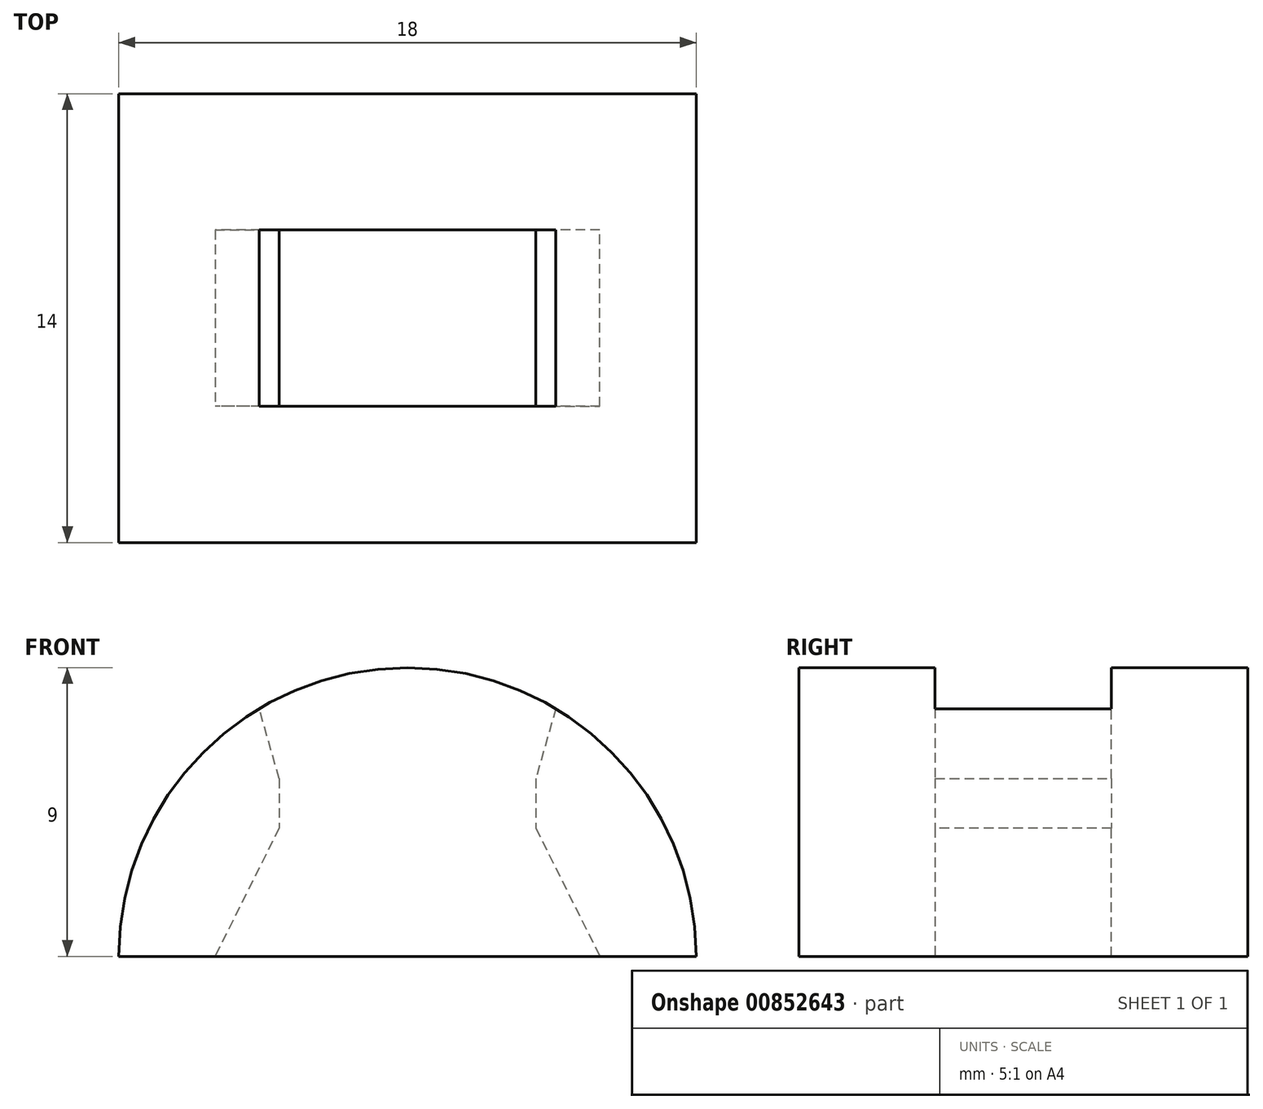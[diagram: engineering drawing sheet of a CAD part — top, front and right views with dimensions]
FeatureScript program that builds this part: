
annotation { "Feature Type Name" : "Feature", "Feature Type Description" : "" }
export const myFeature = defineFeature(function(context is Context, id is Id, definition is map)
    precondition{}
    {
        {
            var Q0;
            Q0=qCreatedBy(makeId("Top.planeOp"),FACE);
            var sketch = newSketch(context, id + "F0", { "sketchPlane" : qUnion([Q0])});
            skLineSegment(sketch, "E0.bottom", {"start": v(9, -7) * mm, "end": v(-9, -7) * mm});
            skLineSegment(sketch, "E0.top", {"start": v(9, 7) * mm, "end": v(-9, 7) * mm});
            skLineSegment(sketch, "E0.left", {"start": v(9, -7) * mm, "end": v(9, 7) * mm});
            skLineSegment(sketch, "E0.right", {"start": v(-9, -7) * mm, "end": v(-9, 7) * mm});
            skPoint(sketch, "E0.middle", {"position": v(0, 0) * mm});
            skLineSegment(sketch, "E1.bottom", {"start": v(4, -2.75) * mm, "end": v(-4, -2.75) * mm});
            skLineSegment(sketch, "E1.top", {"start": v(4, 2.75) * mm, "end": v(-4, 2.75) * mm});
            skLineSegment(sketch, "E1.left", {"start": v(4, -2.75) * mm, "end": v(4, 2.75) * mm});
            skLineSegment(sketch, "E1.right", {"start": v(-4, -2.75) * mm, "end": v(-4, 2.75) * mm});
            skSolve(sketch);
        }
        {
            var Q0;
            Q0=makeQuery(id+"F0.imprint","IMPRINT",FACE,{"disambiguationData":[TD([[makeQuery(id+"F0.imprint","IMPRINT",EDGE,{"derivedFrom":sQuery(id+"F0.wireOp",EDGE,"E0.bottom")}),-1.0]])]});
            extrude(context, id + "F1", {"entities" : qUnion([Q0]), "depth" : 9 * mm, "offsetDistance" : 25 * mm});
        }
        {
            var Q0;
            Q0=qCreatedBy(makeId("Front.planeOp"),FACE);
            var sketch = newSketch(context, id + "F2", { "sketchPlane" : qUnion([Q0])});
            skCircle(sketch, "E2", {"center": v(0, 0) * mm, "radius": 9 * mm});
            skLineSegment(sketch, "E3.bottom", {"start": v(10.05, 9.94) * mm, "end": v(-10.05, 9.94) * mm});
            skLineSegment(sketch, "E3.top", {"start": v(10.05, -9.94) * mm, "end": v(-10.05, -9.94) * mm});
            skLineSegment(sketch, "E3.left", {"start": v(10.05, 9.94) * mm, "end": v(10.05, -9.94) * mm});
            skLineSegment(sketch, "E3.right", {"start": v(-10.05, 9.94) * mm, "end": v(-10.05, -9.94) * mm});
            skSolve(sketch);
        }
        {
            var Q0;
            Q0=makeQuery(id+"F2.imprint","IMPRINT",FACE,{"disambiguationData":[TD([[makeQuery(id+"F2.imprint","IMPRINT",EDGE,{"derivedFrom":sQuery(id+"F2.wireOp",EDGE,"E2")}),-1.0]])]});
            extrude(context, id + "F3", {"entities" : qUnion([Q0]), "operationType" : NewBodyOperationType.REMOVE, "endBound" : BoundingType.SYMMETRIC, "oppositeDirection" : true, "depth" : 25 * mm, "offsetDistance" : 25 * mm});
        }
        {
            var Q0;
            Q0=makeQuery(id+"F1.opExtrude","CAP_EDGE",EDGE,{"disambiguationData":[OSD([sQuery(id+"F0.wireOp",EDGE,"E1.right")])],"isStart":true});
            var Q1;
            Q1=makeQuery(id+"F1.opExtrude","CAP_EDGE",EDGE,{"disambiguationData":[OSD([sQuery(id+"F0.wireOp",EDGE,"E1.left")])],"isStart":true});
            chamfer(context, id + "F4", {"entities" : qUnion([Q0, Q1]), "chamferType" : ChamferType.TWO_OFFSETS, "width1" : 4 * mm, "oppositeDirection" : false, "width2" : 2 * mm, "tangentPropagation" : true});
        }
        {
            var Q0;
            Q0=makeQuery(id+"F3.boolean.opBoolean","INTERSECT",EDGE,{"derivedFrom":[makeQuery(id+"F1.opExtrude","SWEPT_FACE",FACE,{"disambiguationData":[OSD([sQuery(id+"F0.wireOp",EDGE,"E1.right")])]}),makeQuery(id+"F3.opExtrude","SWEPT_FACE",FACE,{"disambiguationData":[OSD([sQuery(id+"F2.wireOp",EDGE,"E2")])]})]});
            var Q1;
            Q1=makeQuery(id+"F3.boolean.opBoolean","INTERSECT",EDGE,{"derivedFrom":[makeQuery(id+"F1.opExtrude","SWEPT_FACE",FACE,{"disambiguationData":[OSD([sQuery(id+"F0.wireOp",EDGE,"E1.left")])]}),makeQuery(id+"F3.opExtrude","SWEPT_FACE",FACE,{"disambiguationData":[OSD([sQuery(id+"F2.wireOp",EDGE,"E2")])]})]});
            chamfer(context, id + "F5", {"entities" : qUnion([Q0, Q1]), "chamferType" : ChamferType.TWO_OFFSETS, "width1" : 0.5 * mm, "oppositeDirection" : false, "width2" : 2.5 * mm, "tangentPropagation" : true});
        }
    });
